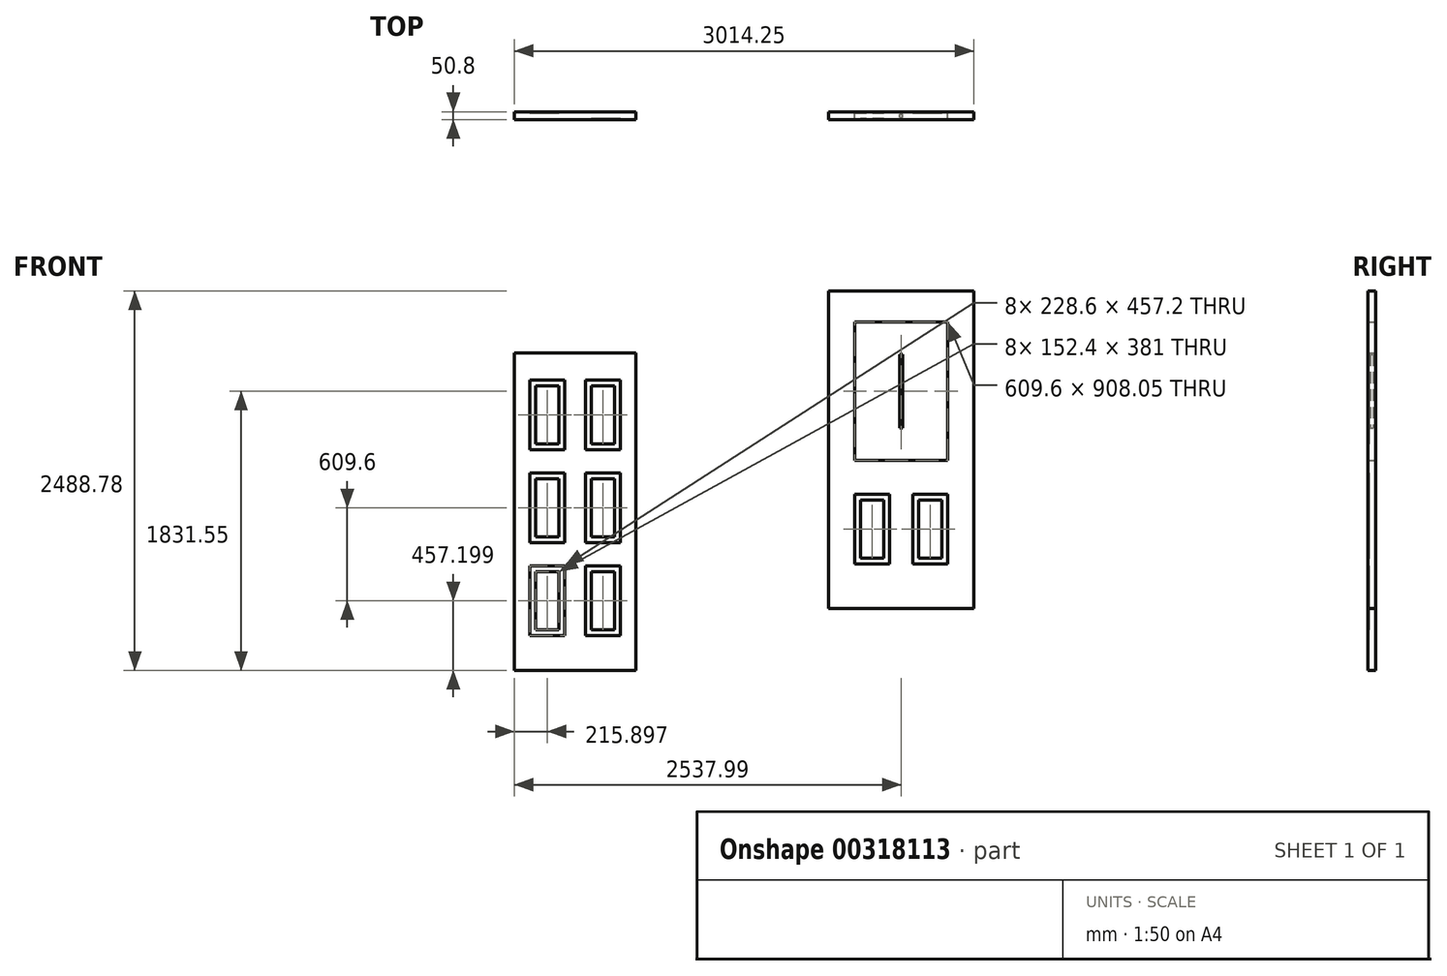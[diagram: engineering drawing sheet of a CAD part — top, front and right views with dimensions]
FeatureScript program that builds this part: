
annotation { "Feature Type Name" : "Feature", "Feature Type Description" : "" }
export const myFeature = defineFeature(function(context is Context, id is Id, definition is map)
    precondition{}
    {
        {
            var Q0;
            Q0=qCreatedBy(makeId("Front.planeOp"),FACE);
            var sketch = newSketch(context, id + "F0", { "sketchPlane" : qUnion([Q0])});
            skLineSegment(sketch, "E0.bottom", {"start": v(-398.46, 2050.23) * mm, "end": v(398.46, 2050.23) * mm});
            skLineSegment(sketch, "E0.top", {"start": v(-398.46, -32.57) * mm, "end": v(398.46, -32.57) * mm});
            skLineSegment(sketch, "E0.left", {"start": v(-398.46, 2050.23) * mm, "end": v(-398.46, -32.57) * mm});
            skLineSegment(sketch, "E0.right", {"start": v(398.46, 2050.23) * mm, "end": v(398.46, -32.57) * mm});
            skPoint(sketch, "E1", {"position": v(0, -32.57) * mm});
            skLineSegment(sketch, "E2.bottom", {"start": v(-296.86, 653.23) * mm, "end": v(-68.26, 653.23) * mm});
            skLineSegment(sketch, "E2.top", {"start": v(-296.86, 196.03) * mm, "end": v(-68.26, 196.03) * mm});
            skLineSegment(sketch, "E2.left", {"start": v(-296.86, 653.23) * mm, "end": v(-296.86, 196.03) * mm});
            skLineSegment(sketch, "E2.right", {"start": v(-68.26, 653.23) * mm, "end": v(-68.26, 196.03) * mm});
            skLineSegment(sketch, "E3.0", {"start": v(-258.76, 615.13) * mm, "end": v(-106.36, 615.13) * mm});
            skLineSegment(sketch, "E3.1", {"start": v(-258.76, 615.13) * mm, "end": v(-258.76, 234.13) * mm});
            skLineSegment(sketch, "E3.2", {"start": v(-258.76, 234.13) * mm, "end": v(-106.36, 234.13) * mm});
            skLineSegment(sketch, "E3.3", {"start": v(-106.36, 615.13) * mm, "end": v(-106.36, 234.13) * mm});
            skLineSegment(sketch, "E4.0.1.0", {"start": v(-68.26, 1262.83) * mm, "end": v(-68.26, 805.63) * mm});
            skLineSegment(sketch, "E4.0.1.1", {"start": v(-296.86, 1262.83) * mm, "end": v(-296.86, 805.63) * mm});
            skLineSegment(sketch, "E4.0.1.2", {"start": v(-296.86, 805.63) * mm, "end": v(-68.26, 805.63) * mm});
            skLineSegment(sketch, "E4.0.1.3", {"start": v(-258.76, 1224.73) * mm, "end": v(-258.76, 843.73) * mm});
            skLineSegment(sketch, "E4.0.1.4", {"start": v(-258.76, 843.73) * mm, "end": v(-106.36, 843.73) * mm});
            skLineSegment(sketch, "E4.0.1.5", {"start": v(-106.36, 1224.73) * mm, "end": v(-106.36, 843.73) * mm});
            skLineSegment(sketch, "E4.0.1.6", {"start": v(-258.76, 1224.73) * mm, "end": v(-106.36, 1224.73) * mm});
            skLineSegment(sketch, "E4.0.1.7", {"start": v(-296.86, 1262.83) * mm, "end": v(-68.26, 1262.83) * mm});
            skLineSegment(sketch, "E4.0.2.0", {"start": v(-68.26, 1872.43) * mm, "end": v(-68.26, 1415.23) * mm});
            skLineSegment(sketch, "E4.0.2.1", {"start": v(-296.86, 1872.43) * mm, "end": v(-296.86, 1415.23) * mm});
            skLineSegment(sketch, "E4.0.2.2", {"start": v(-296.86, 1415.23) * mm, "end": v(-68.26, 1415.23) * mm});
            skLineSegment(sketch, "E4.0.2.3", {"start": v(-258.76, 1834.33) * mm, "end": v(-258.76, 1453.33) * mm});
            skLineSegment(sketch, "E4.0.2.4", {"start": v(-258.76, 1453.33) * mm, "end": v(-106.36, 1453.33) * mm});
            skLineSegment(sketch, "E4.0.2.5", {"start": v(-106.36, 1834.33) * mm, "end": v(-106.36, 1453.33) * mm});
            skLineSegment(sketch, "E4.0.2.6", {"start": v(-258.76, 1834.33) * mm, "end": v(-106.36, 1834.33) * mm});
            skLineSegment(sketch, "E4.0.2.7", {"start": v(-296.86, 1872.43) * mm, "end": v(-68.26, 1872.43) * mm});
            skLineSegment(sketch, "E4.direction1", {"start": v(-296.86, 196.03) * mm, "end": v(425.38, 196.03) * mm, "construction": true});
            skLineSegment(sketch, "E4.direction2", {"start": v(-296.86, 196.03) * mm, "end": v(-296.86, 805.63) * mm, "construction": true});
            skLineSegment(sketch, "E5.MirrorCS", {"start": v(296.86, 653.23) * mm, "end": v(68.26, 653.23) * mm});
            skLineSegment(sketch, "E6.MirrorCS", {"start": v(296.86, 653.23) * mm, "end": v(296.86, 196.03) * mm});
            skLineSegment(sketch, "E7.MirrorCS", {"start": v(258.76, 615.13) * mm, "end": v(106.36, 615.13) * mm});
            skLineSegment(sketch, "E8.MirrorCS", {"start": v(258.76, 1834.33) * mm, "end": v(106.36, 1834.33) * mm});
            skLineSegment(sketch, "E9.MirrorCS", {"start": v(296.86, 1262.83) * mm, "end": v(68.26, 1262.83) * mm});
            skLineSegment(sketch, "E10.MirrorCS", {"start": v(296.86, 1262.83) * mm, "end": v(296.86, 805.63) * mm});
            skLineSegment(sketch, "E11.MirrorCS", {"start": v(296.86, 805.63) * mm, "end": v(68.26, 805.63) * mm});
            skLineSegment(sketch, "E12.MirrorCS", {"start": v(106.36, 1834.33) * mm, "end": v(106.36, 1453.33) * mm});
            skLineSegment(sketch, "E13.MirrorCS", {"start": v(258.76, 1224.73) * mm, "end": v(258.76, 843.73) * mm});
            skLineSegment(sketch, "E14.MirrorCS", {"start": v(296.86, 1415.23) * mm, "end": v(68.26, 1415.23) * mm});
            skLineSegment(sketch, "E15.MirrorCS", {"start": v(258.76, 1224.73) * mm, "end": v(106.36, 1224.73) * mm});
            skLineSegment(sketch, "E16.MirrorCS", {"start": v(296.86, 196.03) * mm, "end": v(68.26, 196.03) * mm});
            skLineSegment(sketch, "E17.MirrorCS", {"start": v(68.26, 653.23) * mm, "end": v(68.26, 196.03) * mm});
            skLineSegment(sketch, "E18.MirrorCS", {"start": v(258.76, 615.13) * mm, "end": v(258.76, 234.13) * mm});
            skLineSegment(sketch, "E19.MirrorCS", {"start": v(258.76, 234.13) * mm, "end": v(106.36, 234.13) * mm});
            skLineSegment(sketch, "E20.MirrorCS", {"start": v(106.36, 1224.73) * mm, "end": v(106.36, 843.73) * mm});
            skLineSegment(sketch, "E21.MirrorCS", {"start": v(258.76, 843.73) * mm, "end": v(106.36, 843.73) * mm});
            skLineSegment(sketch, "E22.MirrorCS", {"start": v(296.86, 196.03) * mm, "end": v(296.86, 805.63) * mm, "construction": true});
            skLineSegment(sketch, "E23.MirrorCS", {"start": v(68.26, 1872.43) * mm, "end": v(68.26, 1415.23) * mm});
            skLineSegment(sketch, "E24.MirrorCS", {"start": v(296.86, 1872.43) * mm, "end": v(68.26, 1872.43) * mm});
            skLineSegment(sketch, "E25.MirrorCS", {"start": v(258.76, 1453.33) * mm, "end": v(106.36, 1453.33) * mm});
            skLineSegment(sketch, "E26.MirrorCS", {"start": v(68.26, 1262.83) * mm, "end": v(68.26, 805.63) * mm});
            skLineSegment(sketch, "E27.MirrorCS", {"start": v(258.76, 1834.33) * mm, "end": v(258.76, 1453.33) * mm});
            skLineSegment(sketch, "E28.MirrorCS", {"start": v(296.86, 1872.43) * mm, "end": v(296.86, 1415.23) * mm});
            skLineSegment(sketch, "E29.MirrorCS", {"start": v(106.36, 615.13) * mm, "end": v(106.36, 234.13) * mm});
            skLineSegment(sketch, "E30.bottom", {"start": v(1663.29, 2456.2) * mm, "end": v(2615.79, 2456.2) * mm});
            skLineSegment(sketch, "E30.top", {"start": v(1663.29, 373.4) * mm, "end": v(2615.79, 373.4) * mm});
            skLineSegment(sketch, "E30.left", {"start": v(1663.29, 2456.2) * mm, "end": v(1663.29, 373.4) * mm});
            skLineSegment(sketch, "E30.right", {"start": v(2615.79, 2456.2) * mm, "end": v(2615.79, 373.4) * mm});
            skPoint(sketch, "E31", {"position": v(2139.54, 373.4) * mm});
            skLineSegment(sketch, "E32.bottom", {"start": v(1834.74, 2253) * mm, "end": v(2444.34, 2253) * mm});
            skLineSegment(sketch, "E32.top", {"start": v(1834.74, 1344.96) * mm, "end": v(2444.34, 1344.96) * mm});
            skLineSegment(sketch, "E32.left", {"start": v(2444.34, 2253) * mm, "end": v(2444.34, 1344.96) * mm});
            skLineSegment(sketch, "E32.right", {"start": v(1834.74, 2253) * mm, "end": v(1834.74, 1344.96) * mm});
            skLineSegment(sketch, "E33.bottom", {"start": v(2130.01, 2253) * mm, "end": v(2149.06, 2253) * mm});
            skLineSegment(sketch, "E33.top", {"start": v(2130.01, 1344.96) * mm, "end": v(2149.06, 1344.96) * mm});
            skLineSegment(sketch, "E33.left", {"start": v(2130.01, 2253) * mm, "end": v(2130.01, 1344.96) * mm});
            skLineSegment(sketch, "E33.right", {"start": v(2149.06, 2253) * mm, "end": v(2149.06, 1344.96) * mm});
            skPoint(sketch, "E34", {"position": v(2139.54, 2253) * mm});
            skLineSegment(sketch, "E35.bottom", {"start": v(1834.74, 1789.46) * mm, "end": v(2444.34, 1789.46) * mm});
            skLineSegment(sketch, "E35.top", {"start": v(1834.74, 1808.5) * mm, "end": v(2444.34, 1808.5) * mm});
            skLineSegment(sketch, "E35.left", {"start": v(2444.34, 1789.46) * mm, "end": v(2444.34, 1808.5) * mm});
            skLineSegment(sketch, "E35.right", {"start": v(1834.74, 1789.46) * mm, "end": v(1834.74, 1808.5) * mm});
            skPoint(sketch, "E36", {"position": v(2444.34, 1798.98) * mm});
            skLineSegment(sketch, "E37.bottom", {"start": v(1834.74, 2040.28) * mm, "end": v(2444.34, 2040.28) * mm});
            skLineSegment(sketch, "E37.top", {"start": v(1834.74, 2021.23) * mm, "end": v(2444.34, 2021.23) * mm});
            skLineSegment(sketch, "E37.left", {"start": v(2444.34, 2040.28) * mm, "end": v(2444.34, 2021.23) * mm});
            skLineSegment(sketch, "E37.right", {"start": v(1834.74, 2040.28) * mm, "end": v(1834.74, 2021.23) * mm});
            skLineSegment(sketch, "E38.bottom", {"start": v(1834.74, 1576.73) * mm, "end": v(2444.34, 1576.73) * mm});
            skLineSegment(sketch, "E38.top", {"start": v(1834.74, 1557.68) * mm, "end": v(2444.34, 1557.68) * mm});
            skLineSegment(sketch, "E38.left", {"start": v(2444.34, 1576.73) * mm, "end": v(2444.34, 1557.68) * mm});
            skLineSegment(sketch, "E38.right", {"start": v(1834.74, 1576.73) * mm, "end": v(1834.74, 1557.68) * mm});
            skPoint(sketch, "E39", {"position": v(2139.54, 2456.2) * mm});
            skLineSegment(sketch, "E40", {"start": v(2139.54, 2400.2) * mm, "end": v(2139.54, 2456.2) * mm});
            skLineSegment(sketch, "E41.0.2.0", {"start": v(2444.34, 1121.53) * mm, "end": v(2444.34, 664.33) * mm});
            skLineSegment(sketch, "E41.0.2.1", {"start": v(2215.74, 1121.53) * mm, "end": v(2215.74, 664.33) * mm});
            skLineSegment(sketch, "E41.0.2.2", {"start": v(2215.74, 664.33) * mm, "end": v(2444.34, 664.33) * mm});
            skLineSegment(sketch, "E41.0.2.7", {"start": v(2215.74, 1121.53) * mm, "end": v(2444.34, 1121.53) * mm});
            skLineSegment(sketch, "E42", {"start": v(2139.54, 373.4) * mm, "end": v(2139.54, 689.04) * mm});
            skLineSegment(sketch, "E43", {"start": v(1834.74, 664.33) * mm, "end": v(2444.34, 664.33) * mm});
            skPoint(sketch, "E44", {"position": v(2139.54, 664.33) * mm});
            skLineSegment(sketch, "E45.0", {"start": v(2253.84, 1083.43) * mm, "end": v(2406.24, 1083.43) * mm});
            skLineSegment(sketch, "E45.1", {"start": v(2253.84, 1083.43) * mm, "end": v(2253.84, 702.43) * mm});
            skLineSegment(sketch, "E45.2", {"start": v(2253.84, 702.43) * mm, "end": v(2406.24, 702.43) * mm});
            skLineSegment(sketch, "E45.3", {"start": v(2406.24, 1083.43) * mm, "end": v(2406.24, 702.43) * mm});
            skLineSegment(sketch, "E46", {"start": v(2139.54, 664.33) * mm, "end": v(2139.54, 580.17) * mm});
            skLineSegment(sketch, "E47.MirrorCS", {"start": v(1872.84, 1083.43) * mm, "end": v(1872.84, 702.43) * mm});
            skLineSegment(sketch, "E48.MirrorCS", {"start": v(2025.24, 702.43) * mm, "end": v(1872.84, 702.43) * mm});
            skLineSegment(sketch, "E49.MirrorCS", {"start": v(2063.34, 1121.53) * mm, "end": v(2063.34, 664.33) * mm});
            skLineSegment(sketch, "E50.MirrorCS", {"start": v(2063.34, 1121.53) * mm, "end": v(1834.74, 1121.53) * mm});
            skLineSegment(sketch, "E51.MirrorCS", {"start": v(2025.24, 1083.43) * mm, "end": v(2025.24, 702.43) * mm});
            skLineSegment(sketch, "E52.MirrorCS", {"start": v(2025.24, 1083.43) * mm, "end": v(1872.84, 1083.43) * mm});
            skLineSegment(sketch, "E53.MirrorCS", {"start": v(2063.34, 664.33) * mm, "end": v(1834.74, 664.33) * mm});
            skLineSegment(sketch, "E54.MirrorCS", {"start": v(1834.74, 1121.53) * mm, "end": v(1834.74, 664.33) * mm});
            skSolve(sketch);
        }
        {
            var Q0;
            Q0=makeQuery(id+"F0.imprint","IMPRINT",FACE,{"disambiguationData":[TD([[makeQuery(id+"F0.imprint","IMPRINT",EDGE,{"derivedFrom":sQuery(id+"F0.wireOp",EDGE,"E0.bottom")}),-1.0]])]});
            var Q1;
            Q1=makeQuery(id+"F0.imprint","IMPRINT",FACE,{"disambiguationData":[TD([[makeQuery(id+"F0.imprint","IMPRINT",EDGE,{"derivedFrom":sQuery(id+"F0.wireOp",EDGE,"E4.0.2.3")}),1.0]])]});
            var Q2;
            Q2=makeQuery(id+"F0.imprint","IMPRINT",FACE,{"disambiguationData":[TD([[makeQuery(id+"F0.imprint","IMPRINT",EDGE,{"derivedFrom":sQuery(id+"F0.wireOp",EDGE,"E8.MirrorCS")}),1.0]])]});
            var Q3;
            Q3=makeQuery(id+"F0.imprint","IMPRINT",FACE,{"disambiguationData":[TD([[makeQuery(id+"F0.imprint","IMPRINT",EDGE,{"derivedFrom":sQuery(id+"F0.wireOp",EDGE,"E13.MirrorCS")}),-1.0]])]});
            var Q4;
            Q4=makeQuery(id+"F0.imprint","IMPRINT",FACE,{"disambiguationData":[TD([[makeQuery(id+"F0.imprint","IMPRINT",EDGE,{"derivedFrom":sQuery(id+"F0.wireOp",EDGE,"E4.0.1.3")}),1.0]])]});
            var Q5;
            Q5=makeQuery(id+"F0.imprint","IMPRINT",FACE,{"disambiguationData":[TD([[makeQuery(id+"F0.imprint","IMPRINT",EDGE,{"derivedFrom":sQuery(id+"F0.wireOp",EDGE,"E3.0")}),-1.0]])]});
            var Q6;
            Q6=makeQuery(id+"F0.imprint","IMPRINT",FACE,{"disambiguationData":[TD([[makeQuery(id+"F0.imprint","IMPRINT",EDGE,{"derivedFrom":sQuery(id+"F0.wireOp",EDGE,"E7.MirrorCS")}),1.0]])]});
            extrude(context, id + "F1", {"entities" : qUnion([Q0, Q1, Q2, Q3, Q4, Q5, Q6]), "endBound" : BoundingType.SYMMETRIC, "depth" : 50.8 * mm});
        }
        {
            var Q0;
            Q0=makeQuery(id+"F0.imprint","IMPRINT",FACE,{"disambiguationData":[TD([[makeQuery(id+"F0.imprint","IMPRINT",EDGE,{"derivedFrom":sQuery(id+"F0.wireOp",EDGE,"E4.0.2.0")}),-1.0]])]});
            var Q1;
            Q1=makeQuery(id+"F0.imprint","IMPRINT",FACE,{"disambiguationData":[TD([[makeQuery(id+"F0.imprint","IMPRINT",EDGE,{"derivedFrom":sQuery(id+"F0.wireOp",EDGE,"E8.MirrorCS")}),-1.0]])]});
            var Q2;
            Q2=makeQuery(id+"F0.imprint","IMPRINT",FACE,{"disambiguationData":[TD([[makeQuery(id+"F0.imprint","IMPRINT",EDGE,{"derivedFrom":sQuery(id+"F0.wireOp",EDGE,"E9.MirrorCS")}),1.0]])]});
            var Q3;
            Q3=makeQuery(id+"F0.imprint","IMPRINT",FACE,{"disambiguationData":[TD([[makeQuery(id+"F0.imprint","IMPRINT",EDGE,{"derivedFrom":sQuery(id+"F0.wireOp",EDGE,"E4.0.1.0")}),-1.0]])]});
            var Q4;
            Q4=makeQuery(id+"F0.imprint","IMPRINT",FACE,{"disambiguationData":[TD([[makeQuery(id+"F0.imprint","IMPRINT",EDGE,{"derivedFrom":sQuery(id+"F0.wireOp",EDGE,"E2.bottom")}),-1.0]])]});
            var Q5;
            Q5=makeQuery(id+"F0.imprint","IMPRINT",FACE,{"disambiguationData":[TD([[makeQuery(id+"F0.imprint","IMPRINT",EDGE,{"derivedFrom":sQuery(id+"F0.wireOp",EDGE,"E5.MirrorCS")}),1.0]])]});
            extrude(context, id + "F2", {"entities" : qUnion([Q0, Q1, Q2, Q3, Q4, Q5]), "operationType" : NewBodyOperationType.ADD, "endBound" : BoundingType.SYMMETRIC, "depth" : 38.1 * mm});
        }
        {
            var Q0;
            {var subQ28=sQuery(id+"F0.wireOp",EDGE,"E30.left");Q0=makeQuery(id+"F0.imprint","IMPRINT",FACE,{"disambiguationData":[TD([[makeQuery(id+"F0.imprint","IMPRINT",EDGE,{"derivedFrom":subQ28}),1.0]])]});}
            var Q1;
            Q1=makeQuery(id+"F0.imprint","IMPRINT",FACE,{"disambiguationData":[TD([[makeQuery(id+"F0.imprint","IMPRINT",EDGE,{"derivedFrom":sQuery(id+"F0.wireOp",EDGE,"E47.MirrorCS")}),1.0]])]});
            var Q2;
            Q2=makeQuery(id+"F0.imprint","IMPRINT",FACE,{"disambiguationData":[TD([[makeQuery(id+"F0.imprint","IMPRINT",EDGE,{"derivedFrom":sQuery(id+"F0.wireOp",EDGE,"E45.0")}),-1.0]])]});
            extrude(context, id + "F3", {"entities" : qUnion([Q0, Q1, Q2]), "endBound" : BoundingType.SYMMETRIC, "depth" : 50.8 * mm});
        }
        {
            var Q0;
            {var subQ0=sQuery(id+"F0.wireOp",EDGE,"E33.bottom");Q0=makeQuery(id+"F0.imprint","IMPRINT",FACE,{"disambiguationData":[TD([[makeQuery(id+"F0.imprint","IMPRINT",EDGE,{"derivedFrom":subQ0}),-1.0]])]});}
            var Q1;
            {var subQ5=sQuery(id+"F0.wireOp",EDGE,"E37.right");Q1=makeQuery(id+"F0.imprint","IMPRINT",FACE,{"disambiguationData":[TD([[makeQuery(id+"F0.imprint","IMPRINT",EDGE,{"derivedFrom":subQ5}),1.0]])]});}
            var Q2;
            {var subQ5=sQuery(id+"F0.wireOp",EDGE,"E37.left");Q2=makeQuery(id+"F0.imprint","IMPRINT",FACE,{"disambiguationData":[TD([[makeQuery(id+"F0.imprint","IMPRINT",EDGE,{"derivedFrom":subQ5}),-1.0]])]});}
            var Q3;
            {var subQ0=sQuery(id+"F0.wireOp",EDGE,"E37.top");var subQ1=sQuery(id+"F0.wireOp",EDGE,"E33.left");var subQ2=makeQuery(id+"F0.imprint","INTERSECT",VERTEX,{"derivedFrom":[subQ1,subQ0]});Q3=makeQuery(id+"F0.imprint","IMPRINT",FACE,{"disambiguationData":[TD([[makeQuery(id+"F0.imprint","IMPRINT",EDGE,{"disambiguationData":[TD([[subQ2,-1.0]])],"derivedFrom":subQ1}),1.0]])]});}
            var Q4;
            {var subQ5=sQuery(id+"F0.wireOp",EDGE,"E35.right");Q4=makeQuery(id+"F0.imprint","IMPRINT",FACE,{"disambiguationData":[TD([[makeQuery(id+"F0.imprint","IMPRINT",EDGE,{"derivedFrom":subQ5}),-1.0]])]});}
            var Q5;
            {var subQ5=sQuery(id+"F0.wireOp",EDGE,"E35.left");Q5=makeQuery(id+"F0.imprint","IMPRINT",FACE,{"disambiguationData":[TD([[makeQuery(id+"F0.imprint","IMPRINT",EDGE,{"derivedFrom":subQ5}),1.0]])]});}
            var Q6;
            {var subQ0=sQuery(id+"F0.wireOp",EDGE,"E35.bottom");var subQ1=sQuery(id+"F0.wireOp",EDGE,"E33.left");var subQ2=makeQuery(id+"F0.imprint","INTERSECT",VERTEX,{"derivedFrom":[subQ1,subQ0]});Q6=makeQuery(id+"F0.imprint","IMPRINT",FACE,{"disambiguationData":[TD([[makeQuery(id+"F0.imprint","IMPRINT",EDGE,{"disambiguationData":[TD([[subQ2,-1.0]])],"derivedFrom":subQ1}),1.0]])]});}
            var Q7;
            {var subQ0=sQuery(id+"F0.wireOp",EDGE,"E33.top");Q7=makeQuery(id+"F0.imprint","IMPRINT",FACE,{"disambiguationData":[TD([[makeQuery(id+"F0.imprint","IMPRINT",EDGE,{"derivedFrom":subQ0}),1.0]])]});}
            var Q8;
            {var subQ5=sQuery(id+"F0.wireOp",EDGE,"E38.left");Q8=makeQuery(id+"F0.imprint","IMPRINT",FACE,{"disambiguationData":[TD([[makeQuery(id+"F0.imprint","IMPRINT",EDGE,{"derivedFrom":subQ5}),-1.0]])]});}
            var Q9;
            {var subQ5=sQuery(id+"F0.wireOp",EDGE,"E38.right");Q9=makeQuery(id+"F0.imprint","IMPRINT",FACE,{"disambiguationData":[TD([[makeQuery(id+"F0.imprint","IMPRINT",EDGE,{"derivedFrom":subQ5}),1.0]])]});}
            var Q10;
            {var subQ0=sQuery(id+"F0.wireOp",EDGE,"E38.bottom");var subQ1=sQuery(id+"F0.wireOp",EDGE,"E33.left");var subQ2=makeQuery(id+"F0.imprint","INTERSECT",VERTEX,{"derivedFrom":[subQ1,subQ0]});Q10=makeQuery(id+"F0.imprint","IMPRINT",FACE,{"disambiguationData":[TD([[makeQuery(id+"F0.imprint","IMPRINT",EDGE,{"disambiguationData":[TD([[subQ2,-1.0]])],"derivedFrom":subQ1}),1.0]])]});}
            var Q11;
            {var subQ0=sQuery(id+"F0.wireOp",EDGE,"E35.top");var subQ1=sQuery(id+"F0.wireOp",EDGE,"E33.left");var subQ2=makeQuery(id+"F0.imprint","INTERSECT",VERTEX,{"derivedFrom":[subQ1,subQ0]});Q11=makeQuery(id+"F0.imprint","IMPRINT",FACE,{"disambiguationData":[TD([[makeQuery(id+"F0.imprint","IMPRINT",EDGE,{"disambiguationData":[TD([[subQ2,-1.0]])],"derivedFrom":subQ1}),1.0]])]});}
            var Q12;
            {var subQ0=sQuery(id+"F0.wireOp",EDGE,"E37.bottom");var subQ1=sQuery(id+"F0.wireOp",EDGE,"E33.left");var subQ2=makeQuery(id+"F0.imprint","INTERSECT",VERTEX,{"derivedFrom":[subQ1,subQ0]});Q12=makeQuery(id+"F0.imprint","IMPRINT",FACE,{"disambiguationData":[TD([[makeQuery(id+"F0.imprint","IMPRINT",EDGE,{"disambiguationData":[TD([[subQ2,-1.0]])],"derivedFrom":subQ1}),1.0]])]});}
            extrude(context, id + "F4", {"entities" : qUnion([Q0, Q1, Q2, Q3, Q4, Q5, Q6, Q7, Q8, Q9, Q10, Q11, Q12]), "operationType" : NewBodyOperationType.ADD, "endBound" : BoundingType.SYMMETRIC, "depth" : 19.05 * mm});
        }
        {
            var Q0;
            Q0=makeQuery(id+"F0.imprint","IMPRINT",FACE,{"disambiguationData":[TD([[makeQuery(id+"F0.imprint","IMPRINT",EDGE,{"derivedFrom":sQuery(id+"F0.wireOp",EDGE,"E47.MirrorCS")}),-1.0]])]});
            var Q1;
            {var subQ1=sQuery(id+"F0.wireOp",EDGE,"E41.0.2.0");Q1=makeQuery(id+"F0.imprint","IMPRINT",FACE,{"disambiguationData":[TD([[makeQuery(id+"F0.imprint","IMPRINT",EDGE,{"derivedFrom":subQ1}),-1.0]])]});}
            extrude(context, id + "F5", {"entities" : qUnion([Q0, Q1]), "operationType" : NewBodyOperationType.ADD, "endBound" : BoundingType.SYMMETRIC, "depth" : 38.1 * mm});
        }
    });
